# Revit family: POT-117_RFA
name_source: partatom
category: Aparatos sanitarios
units: mm (PartAtom-declared; Revit-internal decimal feet)

## family parameters
Activar corte en vistas = No
Compartido = No
Corte con vacíos al cargar = No
Cota de conector redondo = Usar radio
Mantener orientación de anotación = No
Número OmniClass = 23.45.00.00
Punto de cálculo de habitación = No
Se basa en plano de trabajo = No
Siempre vertical = Sí
Tipo de pieza = Normal
Título OmniClass = Sanitary, Laundry, and Cleaning Equipment

## types (1)
- POT-117
    Chrome = Brass Chromed
    Comentarios de tipo = Accessories
    Conexión AC = Sí
    Descripción = Portapapel Potenza
    Elevación por defecto = 0"
    Fabricante = Helvex
    Features = Portapapel que armoniza con la colección de la línea de accesorios Potenza. Montaje oculto, no expone tornillos de fijación. Fácil de instalar.
    Modelo = POT-117
    Total Depth = 1"
    Total Length = 7"
    Total Width = 3"

## geometry (parser evidence)
native form markers: Sweep x3
no freeform markers — native parametric forms only
